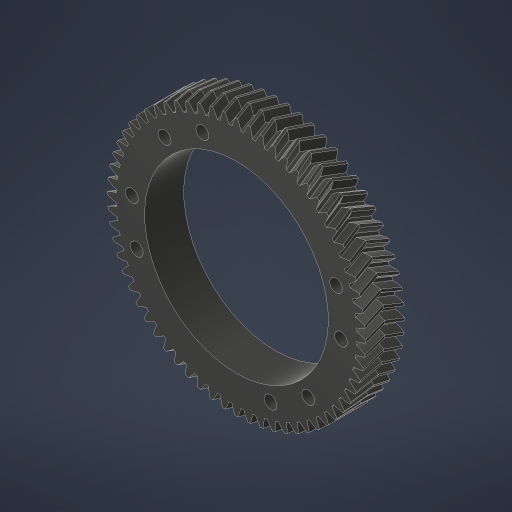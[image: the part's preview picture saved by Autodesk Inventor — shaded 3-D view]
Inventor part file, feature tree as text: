
AUTODESK INVENTOR PART (.ipt)
format: ipt  version: 2023.4 (Build 274418000, 418)  size: 1,743,872 bytes
history: native  units: in
note: dims shown in document units (in); Inventor stores cm internally (conversion verified against a paired STEP export)
features: other x3, sketch x2, hole x2, pattern_circular x1, extrude x1, projected_geometry x1
ambient origin geometry x8: Origin, YZ Plane, XZ Plane, XY Plane, X Axis, Y Axis, Z Axis, Center Point
bodies: Solid1 (feature_tree)
feature tree (10):
  other  "Helical 2M 64T"
  sketch  "Sketch1"  dims[d0=4.7244in d1=3.7in]
  other  "Work Axis1"
  hole  "Hole1"  [1 undecoded]
  pattern_circular  "Circular Pattern1"  Count=4  [1 undecoded]
  extrude  "Extrusion1"  Depth=39.3701in TaperAngle=0.0deg
  other  "DIAMETRIC PITCH"
  hole  "Hole2"  [1 undecoded]
  sketch  "Sketch3"  dims[d2=0.26in d3=29.5276in d4=0.748in d5=0.1969in d6=0.563in d7=39.3701in d8=0.8108in d9=1.5748in d10=2.4737in d12=1.0in d13=0.0in d14=5.0394in d15=1.5in d16=135.0deg d17=0.26in d18=0.38in d19=0.385in d20=0.25in d21=0.5635in d22=1.0in d23=0.8108in d25=2.122in]
  projected_geometry  "Project Cut Edges1"
note: 3 required parameter values undecoded (feature->parameter linkage not recoverable at this tier; creation-order binding heuristic only, values carry confidence <= 0.55)
